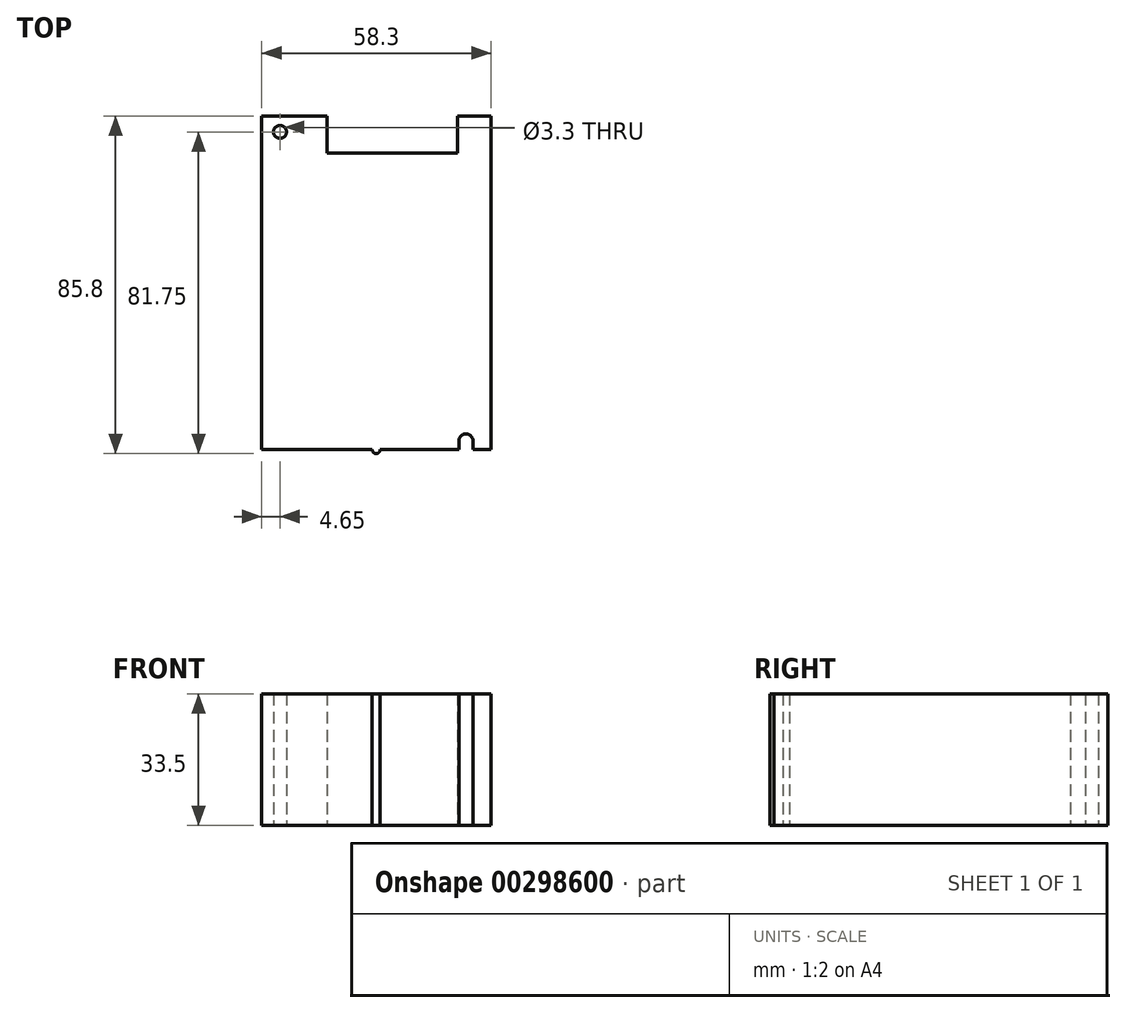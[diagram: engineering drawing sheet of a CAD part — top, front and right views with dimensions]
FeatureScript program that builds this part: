
annotation { "Feature Type Name" : "Feature", "Feature Type Description" : "" }
export const myFeature = defineFeature(function(context is Context, id is Id, definition is map)
    precondition{}
    {
        {
            var Q0;
            Q0=qCreatedBy(makeId("Top.planeOp"),FACE);
            var sketch = newSketch(context, id + "F0", { "sketchPlane" : qUnion([Q0])});
            skLineSegment(sketch, "E0.bottom", {"start": v(-29.1, 41.15) * mm, "end": v(-12.5, 41.15) * mm});
            skLineSegment(sketch, "E0.top", {"start": v(-29.1, -43.65) * mm, "end": v(21, -43.65) * mm});
            skLineSegment(sketch, "E0.left", {"start": v(-29.1, 41.15) * mm, "end": v(-29.1, -43.65) * mm});
            skLineSegment(sketch, "E0.right", {"start": v(29.2, 41.15) * mm, "end": v(29.2, -43.65) * mm});
            skCircle(sketch, "E1", {"center": v(-24.45, 37.1) * mm, "radius": 1.65 * mm});
            skArc(sketch, "E2", {"start": v(24.6, -41.35) * mm, "mid": v(22.8, -39.65) * mm, "end": v(21, -41.35) * mm});
            skLineSegment(sketch, "E3", {"start": v(-12.5, 31.65) * mm, "end": v(20.7, 31.65) * mm});
            skLineSegment(sketch, "E4", {"start": v(20.7, 31.65) * mm, "end": v(20.7, 41.15) * mm});
            skLineSegment(sketch, "E5", {"start": v(-12.5, 31.65) * mm, "end": v(-12.5, 41.15) * mm});
            skLineSegment(sketch, "E6.trimOffspring", {"start": v(20.7, 41.15) * mm, "end": v(29.2, 41.15) * mm});
            skLineSegment(sketch, "E7", {"start": v(21, -41.35) * mm, "end": v(21, -43.65) * mm});
            skLineSegment(sketch, "E8.trimOffspring", {"start": v(24.6, -43.65) * mm, "end": v(29.2, -43.65) * mm});
            skLineSegment(sketch, "E9", {"start": v(24.6, -41.35) * mm, "end": v(24.6, -43.65) * mm});
            skCircle(sketch, "E10", {"center": v(0, -43.65) * mm, "radius": 1 * mm});
            skSolve(sketch);
        }
        {
            var Q0;
            Q0 = qSketchRegion(id + "F0", true);
            extrude(context, id + "F1", {"entities" : qUnion([Q0]), "depth" : 33.5 * mm});
        }
    });
